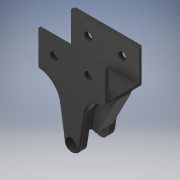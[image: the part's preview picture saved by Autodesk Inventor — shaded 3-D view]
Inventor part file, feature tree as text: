
AUTODESK INVENTOR PART (.ipt)
format: ipt  version: 2019.4 (Build 234330000, 330)  size: 326,144 bytes
history: native  units: mm
features: extrude x4, fillet x4, sketch x2, hole x2
ambient origin geometry x8: Origin, YZ Plane, XZ Plane, XY Plane, X Axis, Y Axis, Z Axis, Center Point
bodies: Solid1 (feature_tree)
feature tree (12):
  sketch  "Sketch1"  dims[d0=45.0mm d1=55.0mm]
  extrude  "Extrusion1"  Depth=55.0mm
  hole  "Hole1"  [1 undecoded]
  extrude  "Extrusion3"  Depth=1.5mm
  extrude  "Extrusion4"  Depth=2.5mm
  extrude  "Extrusion5"  Depth=10.0mm
  fillet  "Fillet1"  Radius=10.0mm
  fillet  "Fillet2"  Radius=10.0mm
  fillet  "Fillet3"  Radius=25.0mm
  fillet  "Fillet4"  Radius=22.0mm
  hole  "Hole2"  [1 undecoded]
  sketch  "Sketch2"  dims[d2=45.0mm d3=20.0mm d4=45.0mm d5=2.5mm d6=10.0mm d7=10.0mm d8=10.0mm d9=25.0mm d10=0.0mm d11=22.0mm d14=8.0mm d15=6.0mm d16=4.0mm d17=2.0mm d18=90.0deg d19=8.0mm d20=20.594885mm d21=10.0mm d22=0.0mm d23=14.0mm d24=0.0mm d25=2.5mm d26=2.5mm d27=20.0mm d28=45.0mm d29=0.0mm d30=1.5mm d31=15.0mm d32=1.5mm d33=1.5mm d34=5.0mm d35=6.0mm d36=4.0mm d37=2.0mm d38=90.0deg d39=8.0mm d40=20.594885mm]
note: 2 required parameter values undecoded (feature->parameter linkage not recoverable at this tier; creation-order binding heuristic only, values carry confidence <= 0.55)
